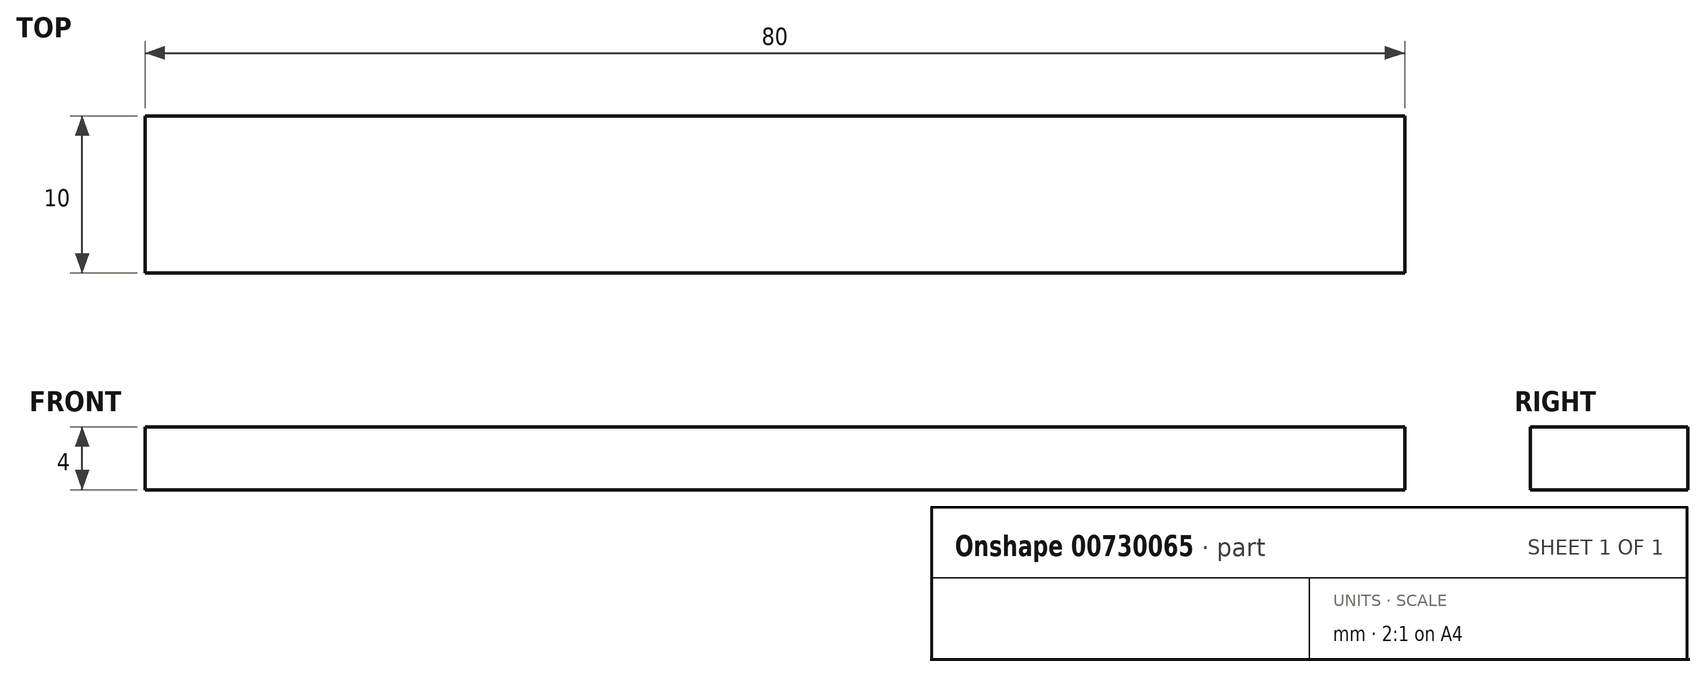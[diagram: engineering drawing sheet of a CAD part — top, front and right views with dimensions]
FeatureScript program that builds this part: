
annotation { "Feature Type Name" : "Feature", "Feature Type Description" : "" }
export const myFeature = defineFeature(function(context is Context, id is Id, definition is map)
    precondition{}
    {
        {
            var Q0;
            Q0=qCreatedBy(makeId("Front.planeOp"),FACE);
            var sketch = newSketch(context, id + "F0", { "sketchPlane" : qUnion([Q0])});
            skLineSegment(sketch, "E0.bottom", {"start": v(0, 0) * mm, "end": v(80, 0) * mm});
            skLineSegment(sketch, "E0.top", {"start": v(0, 4) * mm, "end": v(80, 4) * mm});
            skLineSegment(sketch, "E0.left", {"start": v(0, 0) * mm, "end": v(0, 4) * mm});
            skLineSegment(sketch, "E0.right", {"start": v(80, 0) * mm, "end": v(80, 4) * mm});
            skSolve(sketch);
        }
        {
            var Q0;
            Q0=makeQuery(id+"F0.imprint","IMPRINT",FACE,{"disambiguationData":[TD([[makeQuery(id+"F0.imprint","IMPRINT",EDGE,{"derivedFrom":sQuery(id+"F0.wireOp",EDGE,"E0.bottom")}),1.0]])]});
            extrude(context, id + "F1", {"entities" : qUnion([Q0]), "depth" : 10 * mm, "offsetDistance" : 25 * mm});
        }
    });
